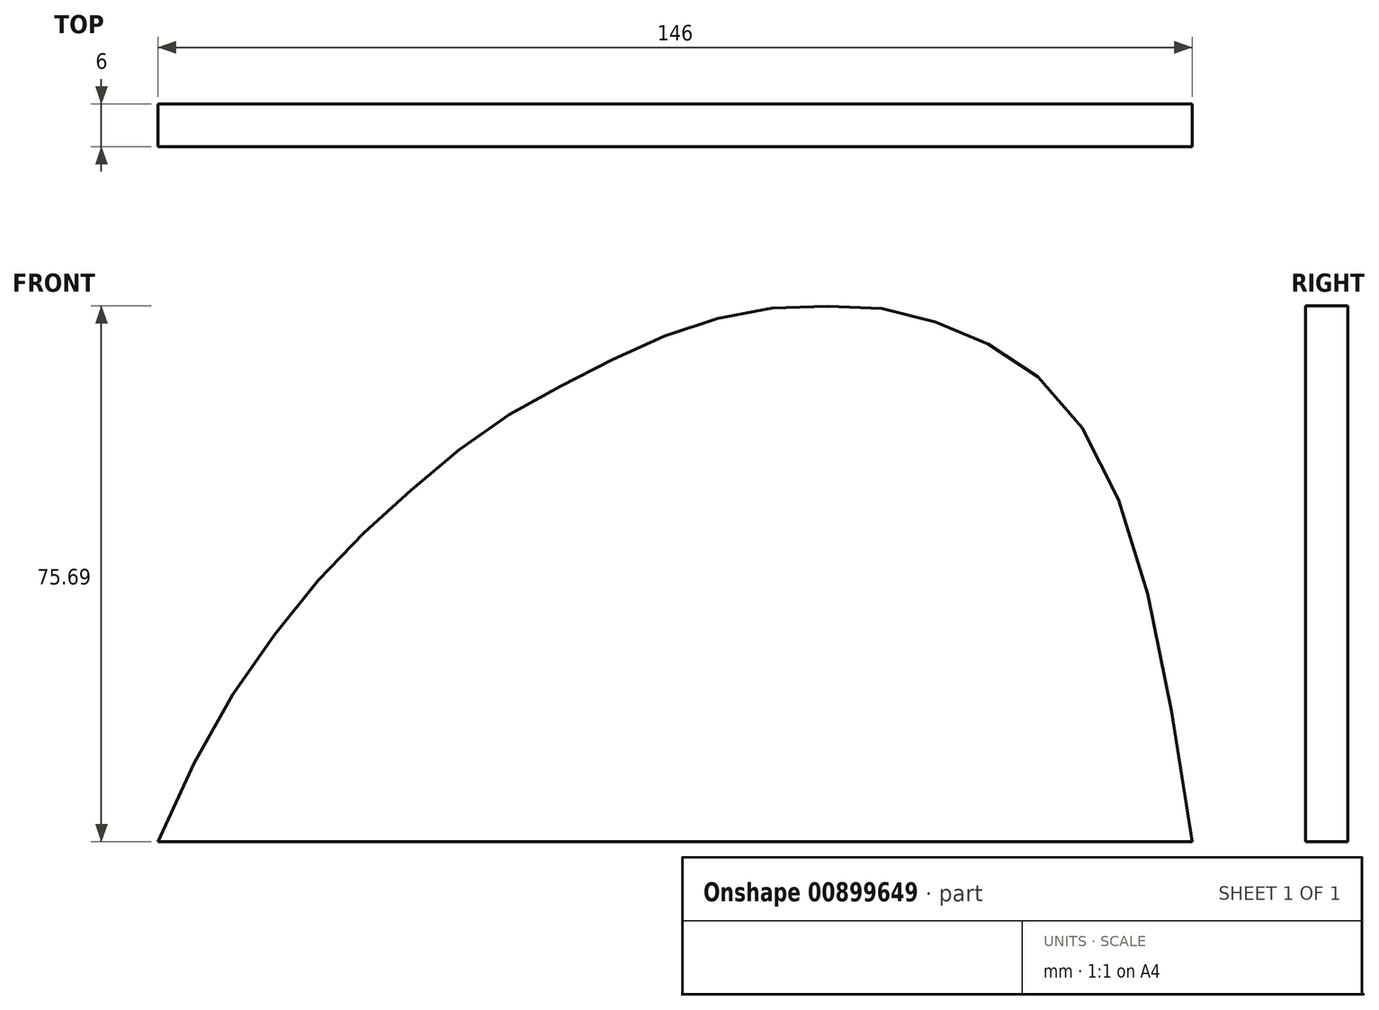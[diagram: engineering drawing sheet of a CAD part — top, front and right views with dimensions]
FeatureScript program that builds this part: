
annotation { "Feature Type Name" : "Feature", "Feature Type Description" : "" }
export const myFeature = defineFeature(function(context is Context, id is Id, definition is map)
    precondition{}
    {
        {
            var Q0;
            Q0=qCreatedBy(makeId("Front.planeOp"),FACE);
            var sketch = newSketch(context, id + "F0", { "sketchPlane" : qUnion([Q0])});
            skLineSegment(sketch, "E0", {"start": v(0, 0) * mm, "end": v(146, 0) * mm});
            skLineSegment(sketch, "E1", {"start": v(0, 0) * mm, "end": v(0, 50.06) * mm, "construction": true});
            skLineSegment(sketch, "E2", {"start": v(0, 0) * mm, "end": v(6.5, 13.87) * mm, "construction": true});
            skLineSegment(sketch, "E3", {"start": v(0, 0) * mm, "end": v(12.97, 24.49) * mm, "construction": true});
            skLineSegment(sketch, "E4", {"start": v(0, 0) * mm, "end": v(19.41, 33.08) * mm, "construction": true});
            skLineSegment(sketch, "E5", {"start": v(0, 0) * mm, "end": v(25.85, 40.51) * mm, "construction": true});
            skLineSegment(sketch, "E6", {"start": v(0, 0) * mm, "end": v(32.27, 46.58) * mm, "construction": true});
            skLineSegment(sketch, "E7", {"start": v(0, 0) * mm, "end": v(38.67, 52.2) * mm, "construction": true});
            skLineSegment(sketch, "E8", {"start": v(0, 0) * mm, "end": v(45.1, 57.28) * mm, "construction": true});
            skLineSegment(sketch, "E9", {"start": v(0, 0) * mm, "end": v(51.5, 61.47) * mm, "construction": true});
            skLineSegment(sketch, "E10", {"start": v(0, 0) * mm, "end": v(57.88, 64.88) * mm, "construction": true});
            skLineSegment(sketch, "E11", {"start": v(0, 0) * mm, "end": v(64.26, 68.16) * mm, "construction": true});
            skLineSegment(sketch, "E12", {"start": v(0, 0) * mm, "end": v(70.66, 71.05) * mm, "construction": true});
            skLineSegment(sketch, "E13", {"start": v(0, 0) * mm, "end": v(77, 73.39) * mm, "construction": true});
            skLineSegment(sketch, "E14", {"start": v(0, 0) * mm, "end": v(83.4, 74.82) * mm, "construction": true});
            skLineSegment(sketch, "E15", {"start": v(0, 0) * mm, "end": v(89.74, 75.65) * mm, "construction": true});
            skLineSegment(sketch, "E16", {"start": v(0, 0) * mm, "end": v(96.32, 75.58) * mm, "construction": true});
            skLineSegment(sketch, "E17", {"start": v(0, 0) * mm, "end": v(102.46, 75.26) * mm, "construction": true});
            skLineSegment(sketch, "E18", {"start": v(0, 0) * mm, "end": v(108.76, 73.72) * mm, "construction": true});
            skLineSegment(sketch, "E19", {"start": v(0, 0) * mm, "end": v(115.09, 71.25) * mm, "construction": true});
            skLineSegment(sketch, "E20", {"start": v(0, 0) * mm, "end": v(121.42, 67.86) * mm, "construction": true});
            skLineSegment(sketch, "E21", {"start": v(0, 0) * mm, "end": v(127.7, 62.14) * mm, "construction": true});
            skLineSegment(sketch, "E22", {"start": v(0, 0) * mm, "end": v(133.94, 52.22) * mm, "construction": true});
            skLineSegment(sketch, "E23", {"start": v(0, 0) * mm, "end": v(140.12, 33.49) * mm, "construction": true});
            skFitSpline(sketch, "E24", {"points": [v(0, 0) * mm, v(6.5, 13.87) * mm, v(12.97, 24.49) * mm, v(19.41, 33.08) * mm, v(25.85, 40.51) * mm, v(32.27, 46.58) * mm, v(38.67, 52.2) * mm, v(45.1, 57.28) * mm, v(51.5, 61.47) * mm, v(57.88, 64.88) * mm, v(64.26, 68.16) * mm, v(70.66, 71.05) * mm, v(77, 73.39) * mm, v(83.4, 74.82) * mm, v(89.74, 75.65) * mm, v(96.32, 75.58) * mm, v(102.46, 75.26) * mm, v(108.76, 73.72) * mm, v(115.09, 71.25) * mm, v(121.42, 67.86) * mm, v(127.7, 62.14) * mm, v(133.94, 52.22) * mm, v(140.12, 33.49) * mm, v(146, 0) * mm], "startDerivative": vector(114.5, 258.68) * mm, "endDerivative": vector(65.19, -430.81) * mm});
            skSolve(sketch);
        }
        {
            var Q0;
            Q0 = qSketchRegion(id + "F0", true);
            extrude(context, id + "F1", {"entities" : qUnion([Q0]), "endBound" : BoundingType.SYMMETRIC, "depth" : 6 * mm, "offsetDistance" : 25 * mm});
        }
    });
